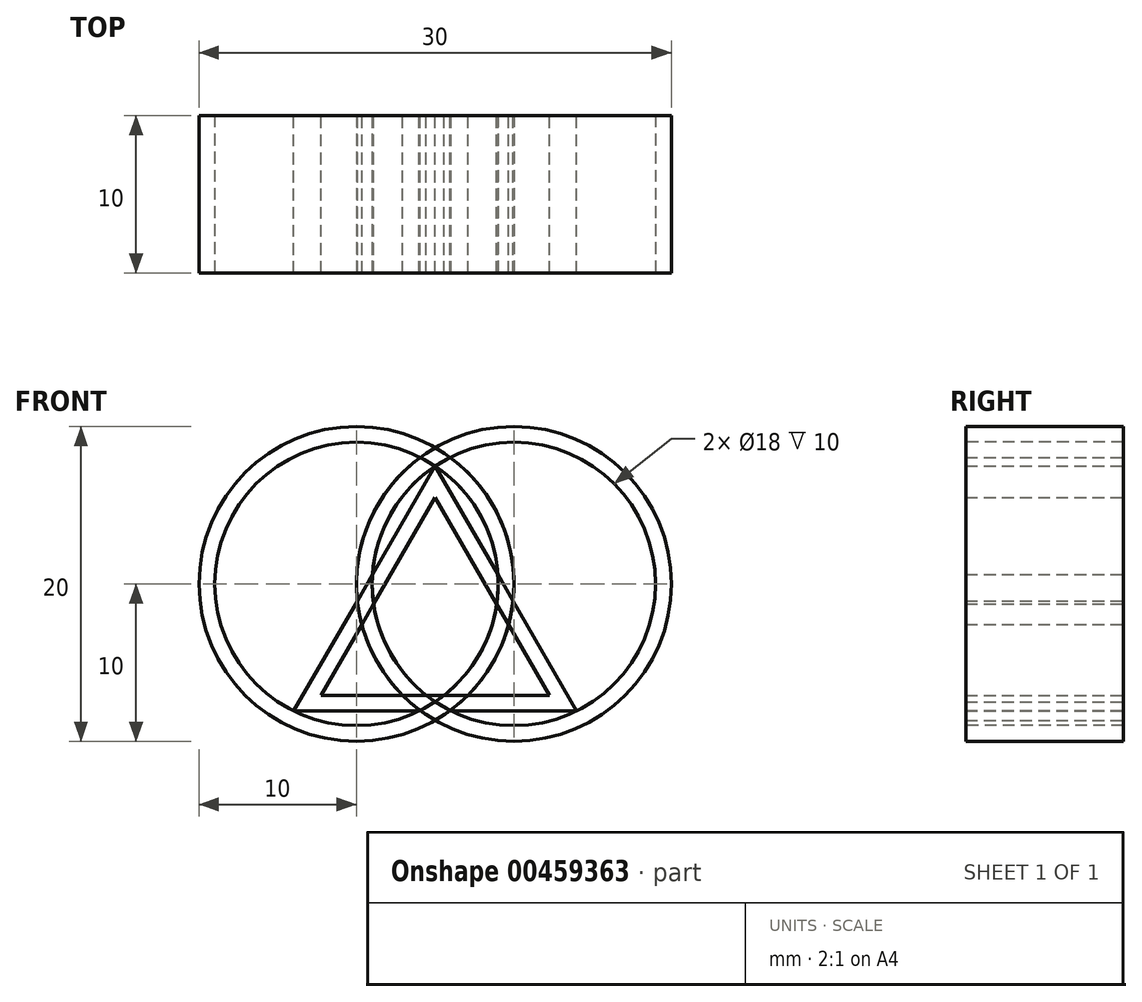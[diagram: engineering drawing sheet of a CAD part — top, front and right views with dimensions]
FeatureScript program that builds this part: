
annotation { "Feature Type Name" : "Feature", "Feature Type Description" : "" }
export const myFeature = defineFeature(function(context is Context, id is Id, definition is map)
    precondition{}
    {
        {
            var Q0;
            Q0=qCreatedBy(makeId("Front.planeOp"),FACE);
            var sketch = newSketch(context, id + "F0", { "sketchPlane" : qUnion([Q0])});
            skLineSegment(sketch, "E0", {"start": v(0, 0) * mm, "end": v(-5, 0) * mm});
            skCircle(sketch, "E1", {"center": v(-5, 0) * mm, "radius": 10 * mm});
            skCircle(sketch, "E2", {"center": v(-5, 0) * mm, "radius": 9 * mm});
            skLineSegment(sketch, "E3", {"start": v(0, 0) * mm, "end": v(5, 0) * mm});
            skCircle(sketch, "E4", {"center": v(5, 0) * mm, "radius": 10 * mm});
            skCircle(sketch, "E5", {"center": v(5, 0) * mm, "radius": 9 * mm});
            skPoint(sketch, "E6.orphan", {"position": v(0, 7.48) * mm});
            skLineSegment(sketch, "E7", {"start": v(8.98, -8.07) * mm, "end": v(-8.98, -8.07) * mm});
            skLineSegment(sketch, "E8", {"start": v(0, 7.48) * mm, "end": v(-8.98, -8.07) * mm});
            skLineSegment(sketch, "E9", {"start": v(8.98, -8.07) * mm, "end": v(0, 7.48) * mm});
            skLineSegment(sketch, "E10", {"start": v(-3.9, -7.07) * mm, "end": v(7.25, -7.07) * mm});
            skLineSegment(sketch, "E11", {"start": v(-5.62, -4.25) * mm, "end": v(-7.25, -7.07) * mm});
            skLineSegment(sketch, "E12", {"start": v(5.24, -3.6) * mm, "end": v(7.25, -7.07) * mm});
            skLineSegment(sketch, "E13", {"start": v(5.24, -3.6) * mm, "end": v(0, 5.48) * mm});
            skLineSegment(sketch, "E14", {"start": v(-5.62, -4.25) * mm, "end": v(0, 5.48) * mm});
            skLineSegment(sketch, "E15", {"start": v(-3.9, -7.07) * mm, "end": v(-7.25, -7.07) * mm});
            skSolve(sketch);
        }
        {
            var Q0;
            {var subQ4=sQuery(id+"F0.wireOp",EDGE,"E4");var subQ5=sQuery(id+"F0.wireOp",EDGE,"E1");var subQ8=makeQuery(id+"F0.imprint","INTERSECT",VERTEX,{"disambiguationData":[OD(0.0)],"derivedFrom":[subQ5,subQ4]});Q0=makeQuery(id+"F0.imprint","IMPRINT",FACE,{"disambiguationData":[TD([[makeQuery(id+"F0.imprint","IMPRINT",EDGE,{"disambiguationData":[TD([[subQ8,1.0]])],"derivedFrom":subQ5}),-1.0]])]});}
            var Q1;
            {var subQ0=sQuery(id+"F0.wireOp",EDGE,"E4");var subQ1=sQuery(id+"F0.wireOp",EDGE,"E1");var subQ2=makeQuery(id+"F0.imprint","INTERSECT",VERTEX,{"disambiguationData":[OD(0.0)],"derivedFrom":[subQ1,subQ0]});Q1=makeQuery(id+"F0.imprint","IMPRINT",FACE,{"disambiguationData":[TD([[makeQuery(id+"F0.imprint","IMPRINT",EDGE,{"disambiguationData":[TD([[subQ2,-1.0]])],"derivedFrom":subQ1}),1.0]])]});}
            var Q2;
            {var subQ13=sQuery(id+"F0.wireOp",EDGE,"E11");Q2=makeQuery(id+"F0.imprint","IMPRINT",FACE,{"disambiguationData":[TD([[makeQuery(id+"F0.imprint","IMPRINT",EDGE,{"derivedFrom":subQ13}),-1.0]])]});}
            var Q3;
            {var subQ8=sQuery(id+"F0.wireOp",EDGE,"E0");var subQ12=sQuery(id+"F0.wireOp",EDGE,"E14");var subQ13=makeQuery(id+"F0.imprint","INTERSECT",VERTEX,{"derivedFrom":[subQ8,subQ12]});Q3=makeQuery(id+"F0.imprint","IMPRINT",FACE,{"disambiguationData":[TD([[makeQuery(id+"F0.imprint","IMPRINT",EDGE,{"disambiguationData":[TD([[subQ13,-1.0]])],"derivedFrom":subQ8}),-1.0]])]});}
            var Q4;
            {var subQ5=sQuery(id+"F0.wireOp",EDGE,"E4");var subQ7=sQuery(id+"F0.wireOp",EDGE,"E0");var subQ8=makeQuery(id+"F0.imprint","INTERSECT",VERTEX,{"derivedFrom":[subQ7,subQ5]});Q4=makeQuery(id+"F0.imprint","IMPRINT",FACE,{"disambiguationData":[TD([[makeQuery(id+"F0.imprint","IMPRINT",EDGE,{"disambiguationData":[TD([[subQ8,1.0]])],"derivedFrom":subQ7}),-1.0]])]});}
            var Q5;
            {var subQ4=sQuery(id+"F0.wireOp",EDGE,"E1");var subQ7=sQuery(id+"F0.wireOp",EDGE,"E3");var subQ8=makeQuery(id+"F0.imprint","INTERSECT",VERTEX,{"derivedFrom":[subQ4,subQ7]});Q5=makeQuery(id+"F0.imprint","IMPRINT",FACE,{"disambiguationData":[TD([[makeQuery(id+"F0.imprint","IMPRINT",EDGE,{"disambiguationData":[TD([[subQ8,-1.0]])],"derivedFrom":subQ4}),1.0]])]});}
            var Q6;
            {var subQ0=sQuery(id+"F0.wireOp",EDGE,"E14");var subQ1=sQuery(id+"F0.wireOp",EDGE,"E4");var subQ2=makeQuery(id+"F0.imprint","INTERSECT",VERTEX,{"derivedFrom":[subQ1,subQ0]});Q6=makeQuery(id+"F0.imprint","IMPRINT",FACE,{"disambiguationData":[TD([[makeQuery(id+"F0.imprint","IMPRINT",EDGE,{"disambiguationData":[TD([[subQ2,-1.0]])],"derivedFrom":subQ1}),1.0]])]});}
            var Q7;
            {var subQ0=sQuery(id+"F0.wireOp",EDGE,"E10");var subQ1=sQuery(id+"F0.wireOp",EDGE,"E1");var subQ2=makeQuery(id+"F0.imprint","INTERSECT",VERTEX,{"derivedFrom":[subQ1,subQ0]});Q7=makeQuery(id+"F0.imprint","IMPRINT",FACE,{"disambiguationData":[TD([[makeQuery(id+"F0.imprint","IMPRINT",EDGE,{"disambiguationData":[TD([[subQ2,-1.0]])],"derivedFrom":subQ1}),1.0]])]});}
            var Q8;
            {var subQ5=sQuery(id+"F0.wireOp",EDGE,"E12");Q8=makeQuery(id+"F0.imprint","IMPRINT",FACE,{"disambiguationData":[TD([[makeQuery(id+"F0.imprint","IMPRINT",EDGE,{"derivedFrom":subQ5}),1.0]])]});}
            var Q9;
            {var subQ0=sQuery(id+"F0.wireOp",EDGE,"E14");var subQ1=sQuery(id+"F0.wireOp",EDGE,"E0");var subQ2=makeQuery(id+"F0.imprint","INTERSECT",VERTEX,{"derivedFrom":[subQ1,subQ0]});Q9=makeQuery(id+"F0.imprint","IMPRINT",FACE,{"disambiguationData":[TD([[makeQuery(id+"F0.imprint","IMPRINT",EDGE,{"disambiguationData":[TD([[subQ2,-1.0]])],"derivedFrom":subQ1}),1.0]])]});}
            var Q10;
            {var subQ0=sQuery(id+"F0.wireOp",EDGE,"E4");var subQ1=sQuery(id+"F0.wireOp",EDGE,"E0");var subQ2=makeQuery(id+"F0.imprint","INTERSECT",VERTEX,{"derivedFrom":[subQ1,subQ0]});Q10=makeQuery(id+"F0.imprint","IMPRINT",FACE,{"disambiguationData":[TD([[makeQuery(id+"F0.imprint","IMPRINT",EDGE,{"disambiguationData":[TD([[subQ2,1.0]])],"derivedFrom":subQ1}),1.0]])]});}
            var Q11;
            {var subQ0=sQuery(id+"F0.wireOp",EDGE,"E3");var subQ1=sQuery(id+"F0.wireOp",EDGE,"E1");var subQ2=makeQuery(id+"F0.imprint","INTERSECT",VERTEX,{"derivedFrom":[subQ1,subQ0]});Q11=makeQuery(id+"F0.imprint","IMPRINT",FACE,{"disambiguationData":[TD([[makeQuery(id+"F0.imprint","IMPRINT",EDGE,{"disambiguationData":[TD([[subQ2,1.0]])],"derivedFrom":subQ1}),1.0]])]});}
            var Q12;
            {var subQ0=sQuery(id+"F0.wireOp",EDGE,"E3");var subQ1=sQuery(id+"F0.wireOp",EDGE,"E2");var subQ2=makeQuery(id+"F0.imprint","INTERSECT",VERTEX,{"derivedFrom":[subQ1,subQ0]});Q12=makeQuery(id+"F0.imprint","IMPRINT",FACE,{"disambiguationData":[TD([[makeQuery(id+"F0.imprint","IMPRINT",EDGE,{"disambiguationData":[TD([[subQ2,1.0]])],"derivedFrom":subQ1}),1.0]])]});}
            var Q13;
            {var subQ0=sQuery(id+"F0.wireOp",EDGE,"E5");var subQ1=sQuery(id+"F0.wireOp",EDGE,"E2");var subQ2=makeQuery(id+"F0.imprint","INTERSECT",VERTEX,{"derivedFrom":[subQ1,subQ0]});Q13=makeQuery(id+"F0.imprint","IMPRINT",FACE,{"disambiguationData":[TD([[makeQuery(id+"F0.imprint","IMPRINT",EDGE,{"disambiguationData":[TD([[subQ2,-1.0]])],"derivedFrom":subQ1}),1.0]])]});}
            var Q14;
            {var subQ1=sQuery(id+"F0.wireOp",EDGE,"E1");var subQ7=sQuery(id+"F0.wireOp",EDGE,"E7");var subQ8=makeQuery(id+"F0.imprint","INTERSECT",VERTEX,{"derivedFrom":[subQ1,subQ7]});Q14=makeQuery(id+"F0.imprint","IMPRINT",FACE,{"disambiguationData":[TD([[makeQuery(id+"F0.imprint","IMPRINT",EDGE,{"disambiguationData":[TD([[subQ8,-1.0]])],"derivedFrom":subQ1}),1.0]])]});}
            extrude(context, id + "F1", {"entities" : qUnion([Q0, Q1, Q2, Q3, Q4, Q5, Q6, Q7, Q8, Q9, Q10, Q11, Q12, Q13, Q14]), "depth" : 10 * mm, "offsetDistance" : 25 * mm});
        }
        {
            var Q0;
            Q0=makeQuery(id+"F1.opExtrude","CAP_FACE",FACE,{"disambiguationData":[OSD([sQuery(id+"F0.wireOp",EDGE,"E1"),sQuery(id+"F0.wireOp",EDGE,"E2"),sQuery(id+"F0.wireOp",EDGE,"E4"),sQuery(id+"F0.wireOp",EDGE,"E7")])],"isStart":false});
            var sketch = newSketch(context, id + "F2", { "sketchPlane" : qUnion([Q0])});
            skLineSegment(sketch, "E16", {"start": v(0, 0) * mm, "end": v(-5, 0) * mm});
            skCircle(sketch, "E17", {"center": v(-5, 0) * mm, "radius": 9 * mm});
            skCircle(sketch, "E18", {"center": v(-5, 0) * mm, "radius": 10 * mm});
            skSolve(sketch);
        }
        {
            var Q0;
            Q0 = qSketchRegion(id + "F2", true);
            extrude(context, id + "F3", {"entities" : qUnion([Q0]), "oppositeDirection" : true, "depth" : 10 * mm, "offsetDistance" : 25 * mm});
        }
        {
            var Q0;
            Q0=makeQuery(id+"F1.opExtrude","CAP_FACE",FACE,{"disambiguationData":[OSD([sQuery(id+"F0.wireOp",EDGE,"E1"),sQuery(id+"F0.wireOp",EDGE,"E4"),sQuery(id+"F0.wireOp",EDGE,"E5"),sQuery(id+"F0.wireOp",EDGE,"E7")])],"isStart":false});
            var sketch = newSketch(context, id + "F4", { "sketchPlane" : qUnion([Q0])});
            skLineSegment(sketch, "E19", {"start": v(0, 0) * mm, "end": v(5, 0) * mm});
            skCircle(sketch, "E20", {"center": v(5, 0) * mm, "radius": 10 * mm});
            skCircle(sketch, "E21", {"center": v(5, 0) * mm, "radius": 9 * mm});
            skSolve(sketch);
        }
        {
            var Q0;
            Q0 = qSketchRegion(id + "F4", true);
            extrude(context, id + "F5", {"entities" : qUnion([Q0]), "oppositeDirection" : true, "depth" : 10 * mm, "offsetDistance" : 25 * mm});
        }
    });
